# Revit family: ARGO-600 AUB04620440001
name_source: partatom
category: Lighting Fixtures
units: mm (PartAtom-declared; Revit-internal decimal feet)

## family parameters
Cut with Voids When Loaded = No
Host = Face
Light Source = Yes
Part Type = Normal
Room Calculation Point = No
Round Connector Dimension = Use Diameter
Shared = No

## types (3) — shared parameters
Apparent Load = 20 VA
Clevertronics_240V Driver = 1330086-A : LED Driver - 20w Stallion, S-MNT
Clevertronics_240V LED Strip = 8002848 : PCA: LED Strip for 2ft Argonaut Tri-Colour (x2)
Clevertronics_Applicable Standards = AS/NZS3820, CISPR15, AS/NZS60598.1
Clevertronics_Construction = Polycarbonate Base and Diffuser with Captive Stainless-Steel Clips (SS301)
Clevertronics_Diffuser = Polycarbonate
Clevertronics_Driver/Ballast = LED Driver – 20w Stallion
Clevertronics_Emergency Driver = 1330086-A : LED Driver - 20w Stallion, S-MNT
Clevertronics_Height = 88 mm  [stored 0.288714 ft]
Clevertronics_IK Rating = IK08
Clevertronics_IP Rating = IP65
Clevertronics_Length = 655 mm  [stored 2.14895 ft]
Clevertronics_MIC Number = AUB04620440001
Clevertronics_Material = Clevertronics_Plycarbonate Base
Clevertronics_Mounting = Surface mount
Clevertronics_Operating Temperature = -25˚C to 40˚C
Clevertronics_Operating Voltage = 240V AC; 50Hz
Clevertronics_Product Description = 240V ARGO 600mm Weatherproof Batten with Switchable Colour
Clevertronics_Weight = 1.25 kg
Clevertronics_Width = 121 mm  [stored 0.396982 ft]
Color Filter = 16777215
Description = 240V ARGO 600mm Weatherproof Batten with Switchable Colour
Dimming Lamp Color Temperature Shift = <None>
Lamp = Dual LED strip module, 3,000K warm white, 5,700K cool white,
50,000h life [L70/B50 Ta 40°C], Ra>80
Manufacturer = Clevertronics
Model = ARGO-600
Tilt Angle = -90.00°
zero-valued in all types: Clevertronics_Annotation Size

## per-type parameters (varying)
| type | Clevertronics_Power Consumption | Clevertronics_Total Lumen Output | Default Elevation | Photometric Web File |
| 3000K | 19W | 1950lm | 1200 mm | 200911ARGO-600 (3000K).ies |
| 4000K | 18W | 2150lm | 1200 mm | 200911 ARGO-600 (4000K).ies |
| 5700K | 19W | 2040lm | 6500 mm  [stored 21.3255 ft] | ARGO-1200_IESA_G_7191283234_03_18.6W_2355lm_350mA_5700K_CIE_202305050904.IES |

note: [stored X ft] marks values corroborated as IEEE doubles in the binary element streams (Revit-internal decimal feet)

## geometry (parser evidence)
native form markers: Blend x2, Sweep x3
no freeform markers — native parametric forms only
